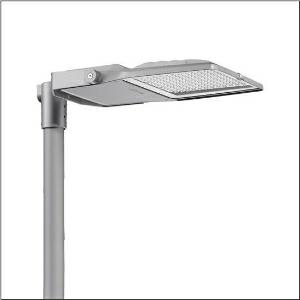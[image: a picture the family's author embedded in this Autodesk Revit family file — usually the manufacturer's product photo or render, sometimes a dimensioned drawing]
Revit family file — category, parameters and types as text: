
# Revit family: floodlight_fl_21_midi___pl43_5xa7781f2a3a_7157
name_source: partatom
category: Lighting Fixtures
units: mm (PartAtom-declared; Revit-internal decimal feet)

## family parameters
Cut with Voids When Loaded = No
Host = Face
Light Source = No
Part Type = Normal
Room Calculation Point = No
Round Connector Dimension = Use Diameter
Shared = No

## types (1)
- --- (1 x LED, 36680 lm, 270.2 W, 3000K)
    Apparent Load = 270 VA
    CIE Flux Codes = 27 78 99 100 100
    Color Rendering = 70
    Color Temperature = 3000K
    Default Elevation = 1800 mm
    Description = Floodlight FL 21 midi, floodlight, primary light control with lens, of PMMA, primary optical cover: protective disc, of toughened safety glass, transparent, light distribution: PL43, light emission: direct distribution, installation type: surface-mounted, LED, High Power LED, rated luminous flux: 36.680lm, luminous efficacy: 135lm/W, light colour: 730, colour temperature: 3000K, control gear: ECG iQ, control: optimised constant luminous flux control (CLO 2.0), Desk-Remote (wireless, voltage-free reading and setting of iQ features in the workshop via application-optimized NFC function/RFID function), Light-Fading, Smart-Wire, Night-Set, Lumen-Switch, Temp-Guard, Auto-Match, with terminal, 6-pole, mains connection: 220..240V, AC, 50/60Hz, start of lifetime: 270W, end of lifetime: 286W, reduction: 135W, luminaire housing, of diecast aluminium, powder-coated, Siteco® metallic grey (DB 702S), corrosivity category C5 according to DIN EN ISO 12944, mast bracket, of steel, galvanised, powder-coated, Siteco® metallic grey (DB 702S), protection rating (complete): IP66, insulation class (complete): insulation class I (protective earthing), certification: CE, protection symbol: D, impact resistance: IK08, permissible operating ambient temperature: -40..+40°C, permissible operating ambient temperature for outdoor applications: -40..+50°C, standard: DIN EN 12944, packaging unit: 1 piece

Light Distribution: PL43
    Height = 76 mm
    Lamp = 1 x LED
    Lamp Light Flux = 36680 lm
    Lamp Power = 270.2 W
    Lamp count = 1
    Length = 657 mm
    Luminous efficacy = 136 lm/W
    Manufacturer = Siteco
    ModVariant = No
    Model = 5XA7781F2A3A
    Number of Poles = 1
    OnlyDefault = Yes
    Power Factor = 1
    Product Name = Floodlight FL 21 midi | PL43
    Product group = floodlight | pylon top
    ProductGroupID = 6101
    Protection Class = Protection class I
    Protection Degree = IP 66
    RLX_Detail_Level = 1
    RlxData = <blob elided: 153401 chars, md5=e9388e0c>
    Socket = socket
    Standby Power = 0 W
    System Light Flux = 36680 lm
    System Power = 270 W
    Type Comments = factory setting: luminous flux: 100 % | dim-lin: 254 | 620 mA
    Type Image = l_1007123.jpg
    URL = http://relux.com
    VarID = @adj_013493
    Voltage = 0 V
    Weight = 0.00 kg
    Width = 442 mm

## geometry (parser evidence)
native form markers: Blend x4, Sweep x15
no freeform markers — native parametric forms only
